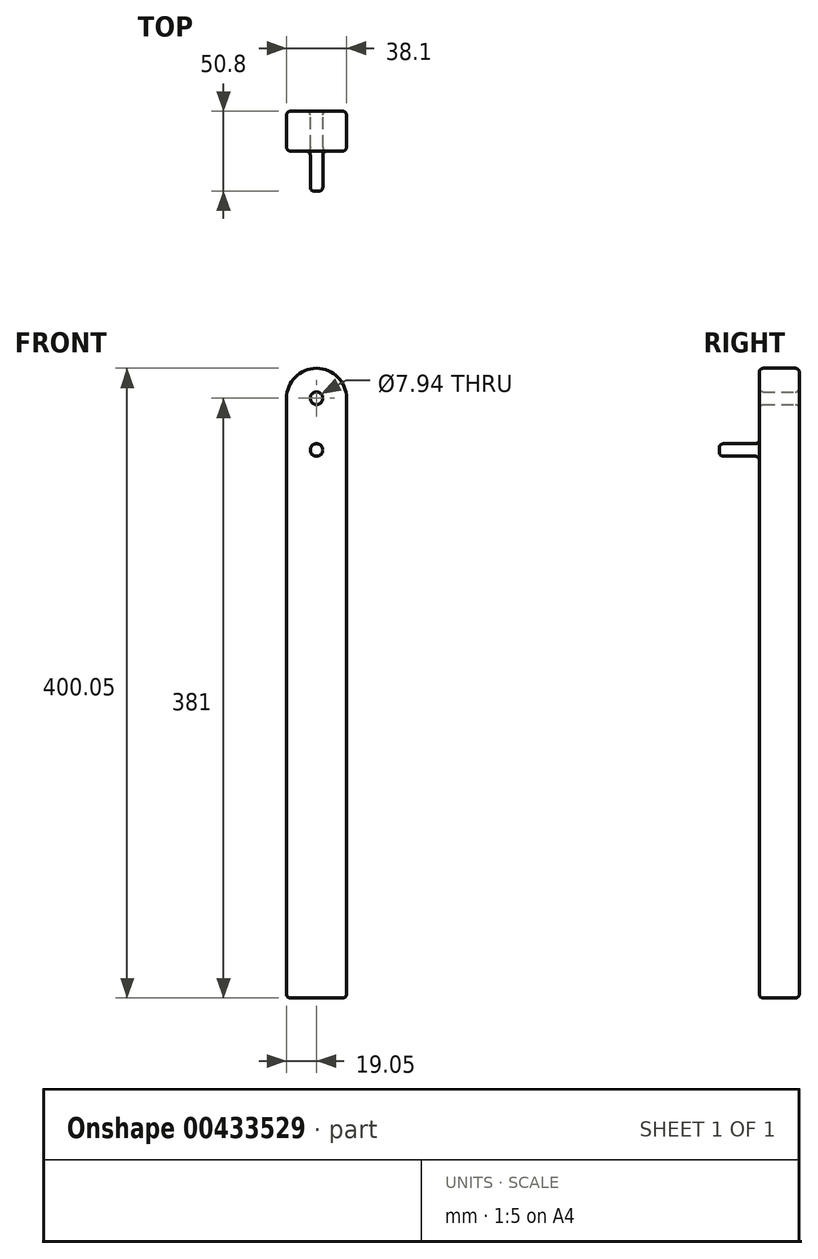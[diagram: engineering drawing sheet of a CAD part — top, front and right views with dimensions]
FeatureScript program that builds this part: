
annotation { "Feature Type Name" : "Feature", "Feature Type Description" : "" }
export const myFeature = defineFeature(function(context is Context, id is Id, definition is map)
    precondition{}
    {
        {
            var Q0;
            Q0=qCreatedBy(makeId("Front.planeOp"),FACE);
            var sketch = newSketch(context, id + "F0", { "sketchPlane" : qUnion([Q0])});
            skLineSegment(sketch, "E0.bottom", {"start": v(0, 0) * mm, "end": v(38.1, 0) * mm});
            skLineSegment(sketch, "E0.left", {"start": v(0, 0) * mm, "end": v(0, 381) * mm});
            skLineSegment(sketch, "E0.right", {"start": v(38.1, 0) * mm, "end": v(38.1, 381) * mm});
            skArc(sketch, "E1", {"start": v(0, 381) * mm, "mid": v(19.05, 400.05) * mm, "end": v(38.1, 381) * mm});
            skCircle(sketch, "E2", {"center": v(19.05, 381) * mm, "radius": 3.97 * mm});
            skCircle(sketch, "E3", {"center": v(19.05, 348.14) * mm, "radius": 3.97 * mm});
            skSolve(sketch);
        }
        {
            var Q0;
            Q0=makeQuery(id+"F0.imprint","IMPRINT",FACE,{"disambiguationData":[TD([[makeQuery(id+"F0.imprint","IMPRINT",EDGE,{"derivedFrom":sQuery(id+"F0.wireOp",EDGE,"E3")}),1.0]])]});
            extrude(context, id + "F1", {"entities" : qUnion([Q0]), "depth" : 50.8 * mm});
        }
        {
            var Q0;
            Q0=makeQuery(id+"F0.imprint","IMPRINT",FACE,{"disambiguationData":[TD([[makeQuery(id+"F0.imprint","IMPRINT",EDGE,{"derivedFrom":sQuery(id+"F0.wireOp",EDGE,"E0.bottom")}),1.0]])]});
            extrude(context, id + "F2", {"entities" : qUnion([Q0]), "operationType" : NewBodyOperationType.ADD, "depth" : 25.4 * mm});
        }
        {
            var Q0;
            Q0=makeQuery(id+"F1.opExtrude","SWEPT_FACE",FACE,{"disambiguationData":[OSD([sQuery(id+"F0.wireOp",EDGE,"E3")])]});
            var Q1;
            Q1=makeQuery(id+"F2.opExtrude","CAP_FACE",FACE,{"disambiguationData":[OSD([sQuery(id+"F0.wireOp",EDGE,"E0.bottom"),sQuery(id+"F0.wireOp",EDGE,"E0.left"),sQuery(id+"F0.wireOp",EDGE,"E0.right"),sQuery(id+"F0.wireOp",EDGE,"E1"),sQuery(id+"F0.wireOp",EDGE,"E2"),sQuery(id+"F0.wireOp",EDGE,"E3")])],"isStart":false});
            var Q2;
            Q2=makeQuery(id+"F2.opExtrude","SWEPT_FACE",FACE,{"disambiguationData":[OSD([sQuery(id+"F0.wireOp",EDGE,"E1")])]});
            var Q3;
            Q3=makeQuery(id+"F2.opExtrude","SWEPT_FACE",FACE,{"disambiguationData":[OSD([sQuery(id+"F0.wireOp",EDGE,"E0.left")])]});
            var Q4;
            Q4=makeQuery(id+"F2.opExtrude","SWEPT_FACE",FACE,{"disambiguationData":[OSD([sQuery(id+"F0.wireOp",EDGE,"E2")])]});
            var Q5;
            Q5=makeQuery(id+"F2.opExtrude","SWEPT_FACE",FACE,{"disambiguationData":[OSD([sQuery(id+"F0.wireOp",EDGE,"E0.right")])]});
            var Q6;
            Q6=makeQuery(id+"F1.opExtrude","CAP_FACE",FACE,{"disambiguationData":[OSD([sQuery(id+"F0.wireOp",EDGE,"E3")])],"isStart":false});
            var Q7;
            Q7=makeQuery(id+"F2.opExtrude","SWEPT_FACE",FACE,{"disambiguationData":[OSD([sQuery(id+"F0.wireOp",EDGE,"E0.bottom")])]});
            var Q8;
            Q8=makeQuery(id+"F2.opExtrude","CAP_EDGE",EDGE,{"disambiguationData":[OSD([sQuery(id+"F0.wireOp",EDGE,"E1")])],"isStart":false});
            var Q9;
            Q9=makeQuery(id+"F2.opExtrude","SWEPT_EDGE",EDGE,{"disambiguationData":[OSD([sQuery(id+"F0.wireOp",EDGE,"E0.right"),sQuery(id+"F0.wireOp",EDGE,"E1")])]});
            var Q10;
            Q10=makeQuery(id+"F2.opExtrude","CAP_EDGE",EDGE,{"disambiguationData":[OSD([sQuery(id+"F0.wireOp",EDGE,"E0.right")])],"isStart":true});
            var Q11;
            Q11=makeQuery(id+"F2.opExtrude","CAP_EDGE",EDGE,{"disambiguationData":[OSD([sQuery(id+"F0.wireOp",EDGE,"E3")])],"isStart":false});
            var Q12;
            Q12=makeQuery(id+"F2.opExtrude","CAP_EDGE",EDGE,{"disambiguationData":[OSD([sQuery(id+"F0.wireOp",EDGE,"E0.bottom")])],"isStart":false});
            var Q13;
            Q13=makeQuery(id+"F2.opExtrude","CAP_EDGE",EDGE,{"disambiguationData":[OSD([sQuery(id+"F0.wireOp",EDGE,"E0.left")])],"isStart":false});
            var Q14;
            {var subQ0=sQuery(id+"F0.wireOp",EDGE,"E3");Q14=makeQuery(id+"F2.boolean.opBoolean","MERGE",FACE,{"derivedFrom":[makeQuery(id+"F1.opExtrude","CAP_FACE",FACE,{"disambiguationData":[OSD([subQ0])],"isStart":true}),makeQuery(id+"F2.opExtrude","CAP_FACE",FACE,{"disambiguationData":[OSD([sQuery(id+"F0.wireOp",EDGE,"E0.bottom"),sQuery(id+"F0.wireOp",EDGE,"E0.left"),sQuery(id+"F0.wireOp",EDGE,"E0.right"),sQuery(id+"F0.wireOp",EDGE,"E1"),sQuery(id+"F0.wireOp",EDGE,"E2"),subQ0])],"isStart":true})]});}
            var Q15;
            Q15=makeQuery(id+"F2.opExtrude","CAP_EDGE",EDGE,{"disambiguationData":[OSD([sQuery(id+"F0.wireOp",EDGE,"E0.right")])],"isStart":false});
            var Q16;
            Q16=makeQuery(id+"F2.opExtrude","CAP_EDGE",EDGE,{"disambiguationData":[OSD([sQuery(id+"F0.wireOp",EDGE,"E0.bottom")])],"isStart":true});
            var Q17;
            Q17=makeQuery(id+"F2.opExtrude","SWEPT_EDGE",EDGE,{"disambiguationData":[OSD([sQuery(id+"F0.wireOp",EDGE,"E0.bottom"),sQuery(id+"F0.wireOp",EDGE,"E0.right")])]});
            var Q18;
            Q18=makeQuery(id+"F2.opExtrude","SWEPT_EDGE",EDGE,{"disambiguationData":[OSD([sQuery(id+"F0.wireOp",EDGE,"E0.left"),sQuery(id+"F0.wireOp",EDGE,"E1")])]});
            var Q19;
            Q19=makeQuery(id+"F2.opExtrude","CAP_EDGE",EDGE,{"disambiguationData":[OSD([sQuery(id+"F0.wireOp",EDGE,"E0.left")])],"isStart":true});
            var Q20;
            Q20=makeQuery(id+"F2.opExtrude","CAP_EDGE",EDGE,{"disambiguationData":[OSD([sQuery(id+"F0.wireOp",EDGE,"E2")])],"isStart":false});
            var Q21;
            Q21=makeQuery(id+"F2.opExtrude","SWEPT_EDGE",EDGE,{"disambiguationData":[OSD([sQuery(id+"F0.wireOp",EDGE,"E0.bottom"),sQuery(id+"F0.wireOp",EDGE,"E0.left")])]});
            var Q22;
            Q22=makeQuery(id+"F1.opExtrude","CAP_EDGE",EDGE,{"disambiguationData":[OSD([sQuery(id+"F0.wireOp",EDGE,"E3")])],"isStart":false});
            var Q23;
            Q23=makeQuery(id+"F2.opExtrude","CAP_EDGE",EDGE,{"disambiguationData":[OSD([sQuery(id+"F0.wireOp",EDGE,"E2")])],"isStart":true});
            var Q24;
            Q24=makeQuery(id+"F2.opExtrude","CAP_EDGE",EDGE,{"disambiguationData":[OSD([sQuery(id+"F0.wireOp",EDGE,"E1")])],"isStart":true});
            fillet(context, id + "F3", {"entities" : qUnion([Q0, Q1, Q2, Q3, Q4, Q5, Q6, Q7, Q8, Q9, Q10, Q11, Q12, Q13, Q14, Q15, Q16, Q17, Q18, Q19, Q20, Q21, Q22, Q23, Q24]), "radius" : 2.54 * mm, "tangentPropagation" : true, "allowEdgeOverflow" : false});
        }
    });
